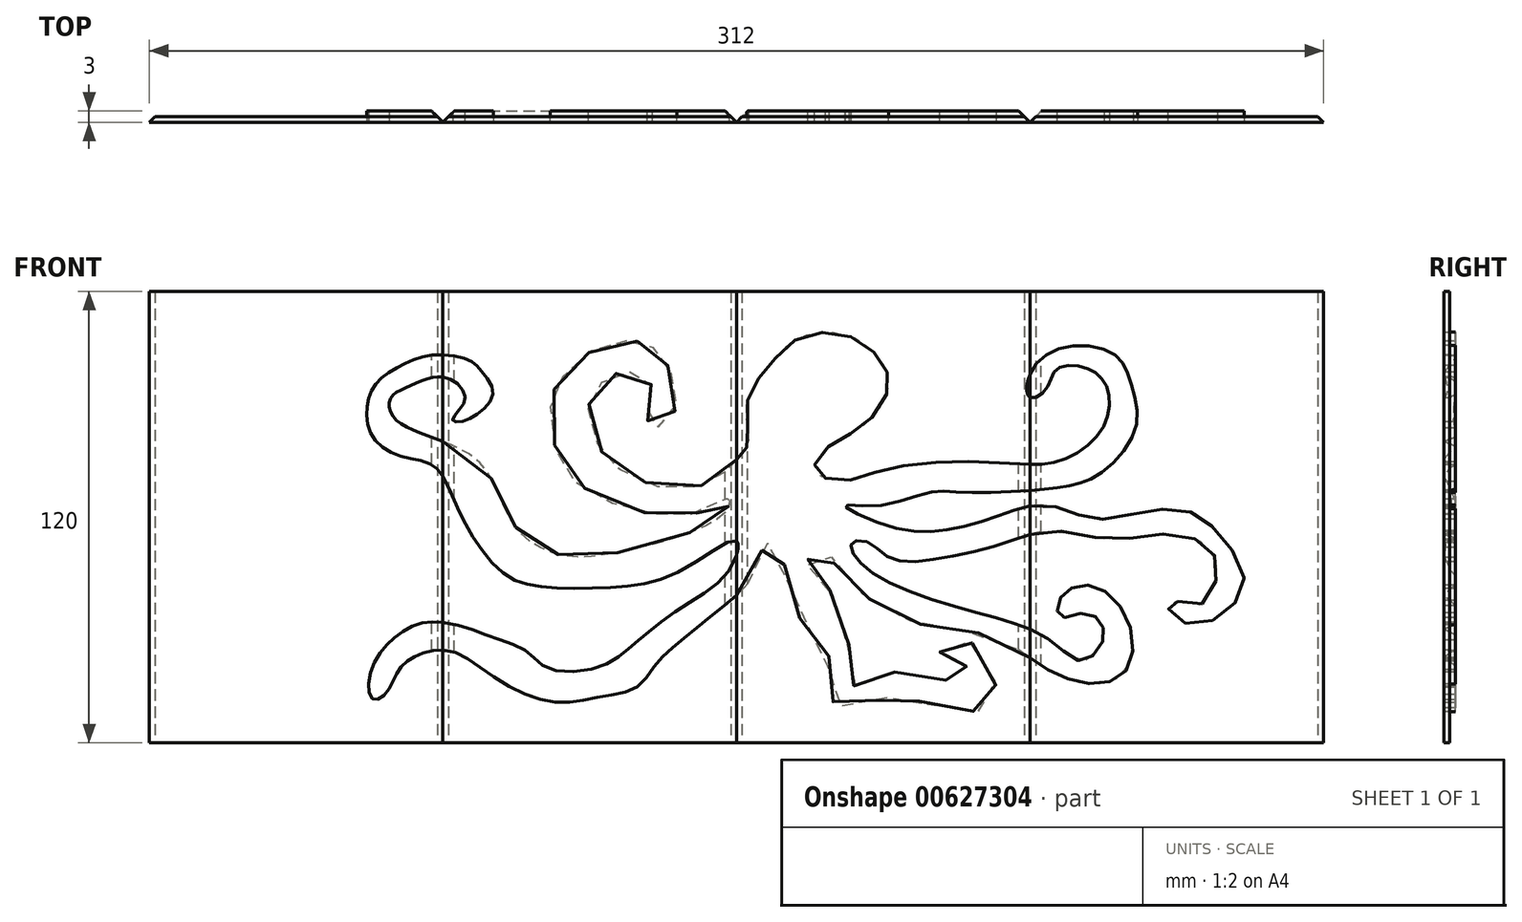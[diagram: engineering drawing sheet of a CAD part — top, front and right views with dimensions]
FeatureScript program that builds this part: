
annotation { "Feature Type Name" : "Feature", "Feature Type Description" : "" }
export const myFeature = defineFeature(function(context is Context, id is Id, definition is map)
    precondition{}
    {
        {
            var Q0;
            Q0=qCreatedBy(makeId("Top.planeOp"),FACE);
            var sketch = newSketch(context, id + "F0", { "sketchPlane" : qUnion([Q0])});
            skLineSegment(sketch, "E0", {"start": v(-73.98, 9.57) * mm, "end": v(1.02, 9.57) * mm});
            skLineSegment(sketch, "E1", {"start": v(1.02, 9.57) * mm, "end": v(2.52, 8.07) * mm});
            skLineSegment(sketch, "E2", {"start": v(2.52, 8.07) * mm, "end": v(-75.48, 8.07) * mm});
            skLineSegment(sketch, "E3", {"start": v(-75.48, 8.07) * mm, "end": v(-73.98, 9.57) * mm});
            skLineSegment(sketch, "E4.1.0.0", {"start": v(4.02, 9.57) * mm, "end": v(79.02, 9.57) * mm});
            skLineSegment(sketch, "E4.1.0.1", {"start": v(80.52, 8.07) * mm, "end": v(2.52, 8.07) * mm});
            skLineSegment(sketch, "E4.1.0.2", {"start": v(79.02, 9.57) * mm, "end": v(80.52, 8.07) * mm});
            skLineSegment(sketch, "E4.1.0.3", {"start": v(2.52, 8.07) * mm, "end": v(4.02, 9.57) * mm});
            skLineSegment(sketch, "E4.2.0.0", {"start": v(82.02, 9.57) * mm, "end": v(157.02, 9.57) * mm});
            skLineSegment(sketch, "E4.2.0.1", {"start": v(158.52, 8.07) * mm, "end": v(80.52, 8.07) * mm});
            skLineSegment(sketch, "E4.2.0.2", {"start": v(157.02, 9.57) * mm, "end": v(158.52, 8.07) * mm});
            skLineSegment(sketch, "E4.2.0.3", {"start": v(80.52, 8.07) * mm, "end": v(82.02, 9.57) * mm});
            skLineSegment(sketch, "E4.3.0.0", {"start": v(160.02, 9.57) * mm, "end": v(235.02, 9.57) * mm});
            skLineSegment(sketch, "E4.3.0.1", {"start": v(236.52, 8.07) * mm, "end": v(158.52, 8.07) * mm});
            skLineSegment(sketch, "E4.3.0.2", {"start": v(235.02, 9.57) * mm, "end": v(236.52, 8.07) * mm});
            skLineSegment(sketch, "E4.3.0.3", {"start": v(158.52, 8.07) * mm, "end": v(160.02, 9.57) * mm});
            skLineSegment(sketch, "E4.direction1", {"start": v(-75.48, 8.07) * mm, "end": v(2.52, 8.07) * mm, "construction": true});
            skSolve(sketch);
        }
        {
            var Q0;
            Q0=makeQuery(id+"F0.imprint","IMPRINT",FACE,{"disambiguationData":[TD([[makeQuery(id+"F0.imprint","IMPRINT",EDGE,{"derivedFrom":sQuery(id+"F0.wireOp",EDGE,"E0")}),-1.0]])]});
            extrude(context, id + "F1", {"entities" : qUnion([Q0]), "depth" : 120 * mm, "offsetDistance" : 25 * mm});
        }
        {
            var Q0;
            Q0=makeQuery(id+"F0.imprint","IMPRINT",FACE,{"disambiguationData":[TD([[makeQuery(id+"F0.imprint","IMPRINT",EDGE,{"derivedFrom":sQuery(id+"F0.wireOp",EDGE,"E4.1.0.0")}),-1.0]])]});
            extrude(context, id + "F2", {"entities" : qUnion([Q0]), "depth" : 120 * mm, "offsetDistance" : 25 * mm});
        }
        {
            var Q0;
            Q0=makeQuery(id+"F0.imprint","IMPRINT",FACE,{"disambiguationData":[TD([[makeQuery(id+"F0.imprint","IMPRINT",EDGE,{"derivedFrom":sQuery(id+"F0.wireOp",EDGE,"E4.2.0.0")}),-1.0]])]});
            extrude(context, id + "F3", {"entities" : qUnion([Q0]), "depth" : 120 * mm, "offsetDistance" : 25 * mm});
        }
        {
            var Q0;
            Q0=makeQuery(id+"F0.imprint","IMPRINT",FACE,{"disambiguationData":[TD([[makeQuery(id+"F0.imprint","IMPRINT",EDGE,{"derivedFrom":sQuery(id+"F0.wireOp",EDGE,"E4.3.0.0")}),-1.0]])]});
            extrude(context, id + "F4", {"entities" : qUnion([Q0]), "depth" : 120 * mm, "offsetDistance" : 25 * mm});
        }
        {
            var Q0;
            Q0=makeQuery(id+"F3.opExtrude","SWEPT_FACE",FACE,{"disambiguationData":[OSD([sQuery(id+"F0.wireOp",EDGE,"E4.2.0.1")])]});
            var sketch = newSketch(context, id + "F5", { "sketchPlane" : qUnion([Q0])});
            skPoint(sketch, "E5.174.internal.snap0", {"position": v(158.52, 60) * mm});
            skFitSpline(sketch, "E5", {"points": [v(83.62, 79.52) * mm, v(82.23, 77.34) * mm, v(78.27, 72.79) * mm, v(73.72, 69.42) * mm, v(65.4, 67.24) * mm, v(54.5, 70.02) * mm, v(46.38, 75.17) * mm, v(42.82, 81.7) * mm, v(41.23, 89.63) * mm, v(43.8, 94.78) * mm, v(48.36, 98.14) * mm, v(54.3, 98.34) * mm, v(57.67, 95.77) * mm, v(58.07, 91.21) * mm, v(56.88, 87.05) * mm, v(57.67, 84.28) * mm, v(61.83, 84.67) * mm, v(64.6, 90.22) * mm, v(63.61, 97.35) * mm, v(60.64, 102.9) * mm, v(56.68, 106.07) * mm, v(51.14, 106.86) * mm, v(42.82, 104.68) * mm, v(35.49, 98.54) * mm, v(31.72, 93) * mm, v(31.33, 83.29) * mm, v(34.9, 72.4) * mm, v(41.23, 67.04) * mm, v(54.1, 61.5) * mm, v(63.81, 60.9) * mm, v(71.93, 61.7) * mm, v(78.27, 64.87) * mm, v(78.07, 62.1) * mm, v(73.12, 58.13) * mm, v(63.22, 54.17) * mm, v(44.4, 49.81) * mm, v(34.3, 49.81) * mm, v(26.18, 53.18) * mm, v(20.83, 58.92) * mm, v(16.47, 67.84) * mm, v(10.73, 75.96) * mm, v(-2.74, 82.1) * mm, v(-10.87, 86.96) * mm, v(-11.39, 91.6) * mm, v(-7.34, 94.43) * mm, v(0, 97.18) * mm, v(5.4, 96.18) * mm, v(8.39, 91.93) * mm, v(6.64, 88.19) * mm, v(5.14, 85.7) * mm, v(7.64, 85.44) * mm, v(12.63, 88.19) * mm, v(15.88, 93.18) * mm, v(12.63, 98.93) * mm, v(9.59, 101.74) * mm, v(0, 103.13) * mm, v(-8.62, 100.35) * mm, v(-15.15, 95.6) * mm, v(-17.53, 89.67) * mm, v(-16.54, 82.15) * mm, v(-9.41, 76.4) * mm, v(0, 73.64) * mm, v(5.03, 65.52) * mm, v(9.98, 55.63) * mm, v(19.28, 44.54) * mm, v(30.17, 41.38) * mm, v(48.58, 41.38) * mm, v(66.39, 46.13) * mm, v(80.52, 53.65) * mm, v(78.4, 45.58) * mm, v(68.32, 37.53) * mm, v(57.42, 29.71) * mm, v(51.37, 24.58) * mm, v(43.73, 20.04) * mm, v(30.36, 19.8) * mm, v(25.1, 24.1) * mm, v(17.46, 27.45) * mm, v(8.15, 30.79) * mm, v(-2.12, 31.98) * mm, v(-10.95, 27.45) * mm, v(-16.68, 18.61) * mm, v(-16.2, 11.69) * mm, v(-12.86, 12.88) * mm, v(-9.52, 18.85) * mm, v(-4.98, 22.9) * mm, v(3.61, 24.58) * mm, v(11.73, 20.52) * mm, v(24.39, 12.88) * mm, v(35.61, 10.73) * mm, v(45.16, 12.4) * mm, v(54, 14.8) * mm, v(59.49, 21.24) * mm, v(66.41, 27.69) * mm, v(77.64, 36.76) * mm, v(85.04, 44.64) * mm, v(87.67, 51.8) * mm, v(89.82, 53.24) * mm, v(92.92, 48.7) * mm, v(95.07, 37) * mm, v(99.6, 31.03) * mm, v(104.86, 25.06) * mm, v(104.14, 16.7) * mm, v(106.05, 10.97) * mm, v(114.65, 9.54) * mm, v(120.86, 12.16) * mm, v(125.63, 12.64) * mm, v(130.89, 10.25) * mm, v(141.15, 8.58) * mm, v(148.08, 9.06) * mm, v(149.51, 14.07) * mm, v(147.84, 20.76) * mm, v(142.35, 26.97) * mm, v(137.1, 26.5) * mm, v(134.7, 24.58) * mm, v(134.95, 22.43) * mm, v(139.48, 22.43) * mm, v(142.11, 18.13) * mm, v(140.44, 15.03) * mm, v(134.23, 17.66) * mm, v(125.16, 19.33) * mm, v(118.23, 16.7) * mm, v(112.74, 14.8) * mm, v(109.4, 18.37) * mm, v(110.35, 25.06) * mm, v(108.2, 35.09) * mm, v(102.95, 43.2) * mm, v(99.84, 45.12) * mm, v(100.56, 51.09) * mm, v(104.14, 51.33) * mm, v(107.25, 46.31) * mm, v(112.98, 40.34) * mm, v(120.86, 35.09) * mm, v(131.36, 31.03) * mm, v(142.35, 29.6) * mm, v(152.38, 26.73) * mm, v(161.93, 20.28) * mm, v(173.87, 15.75) * mm, v(183.9, 18.97) * mm, v(185.01, 31.44) * mm, v(176.98, 41.13) * mm, v(169.5, 41.13) * mm, v(165.9, 36.98) * mm, v(166.73, 33.37) * mm, v(173.1, 34.48) * mm, v(177.53, 31.71) * mm, v(177.81, 26.73) * mm, v(172.55, 21.74) * mm, v(165.35, 26.17) * mm, v(155.38, 31.44) * mm, v(136.82, 36.7) * mm, v(116.88, 45) * mm, v(111.34, 50.82) * mm, v(111.34, 53.32) * mm, v(115.5, 53.32) * mm, v(121.31, 49.16) * mm, v(132.11, 48.6) * mm, v(150.67, 52.76) * mm, v(164.8, 56.36) * mm, v(180.3, 54.15) * mm, v(195.81, 55.53) * mm, v(206.61, 51.38) * mm, v(208, 43.34) * mm, v(202.74, 36.42) * mm, v(195.81, 37.8) * mm, v(195.81, 34.48) * mm, v(203.01, 31.44) * mm, v(212.43, 36.42) * mm, v(215.2, 45.28) * mm, v(207.72, 56.64) * mm, v(200.52, 61.62) * mm, v(188.06, 61.35) * mm, v(176.98, 59.4) * mm, v(169.23, 61.35) * mm, v(161.2, 63.29) * mm, v(149, 60) * mm, v(134.88, 56.36) * mm, v(120.48, 57.75) * mm, v(109.4, 63) * mm, v(117.71, 63) * mm, v(132.11, 66.6) * mm, v(139.31, 66.6) * mm, v(155.93, 66.89) * mm, v(168.67, 68.27) * mm, v(177.26, 71.6) * mm, v(186.67, 83.78) * mm, v(185.29, 95.69) * mm, v(181.13, 103.17) * mm, v(167.29, 105.1) * mm, v(158.52, 97.9) * mm, v(158.52, 91.81) * mm, v(162.86, 94.03) * mm, v(165.62, 99.29) * mm, v(173.66, 99.57) * mm, v(178.92, 94.58) * mm, v(178.09, 84.06) * mm, v(166.18, 74.92) * mm, v(151.5, 74.36) * mm, v(135.16, 74.64) * mm, v(118.82, 72.42) * mm, v(108.57, 69.66) * mm, v(101.37, 72.42) * mm, v(104.7, 78.52) * mm, v(113.84, 84.06) * mm, v(120.76, 93.75) * mm, v(119.1, 101.5) * mm, v(109.68, 108.43) * mm, v(96.66, 107.32) * mm, v(88.36, 99.29) * mm, v(83.37, 90.43) * mm, v(83.62, 79.52) * mm]});
            skSolve(sketch);
        }
        {
            var Q0;
            Q0=qSketchRegion(id+"F5",true);
            extrude(context, id + "F6", {"entities" : qUnion([Q0]), "oppositeDirection" : true, "depth" : 3 * mm, "offsetDistance" : 25 * mm});
        }
        {
            var Q0;
            Q0=makeQuery(id+"F2.opExtrude","CAP_FACE",FACE,{"disambiguationData":[OSD([sQuery(id+"F0.wireOp",EDGE,"E4.1.0.0"),sQuery(id+"F0.wireOp",EDGE,"E4.1.0.1"),sQuery(id+"F0.wireOp",EDGE,"E4.1.0.2"),sQuery(id+"F0.wireOp",EDGE,"E4.1.0.3")])],"isStart":false});
            var sketch = newSketch(context, id + "F7", { "sketchPlane" : qUnion([Q0])});
            skLineSegment(sketch, "E6", {"start": v(2.52, 8.07) * mm, "end": v(7.01, 12.56) * mm});
            skLineSegment(sketch, "E7", {"start": v(2.52, 8.07) * mm, "end": v(-1.98, 12.56) * mm});
            skLineSegment(sketch, "E8", {"start": v(-1.98, 12.56) * mm, "end": v(7.01, 12.56) * mm});
            skLineSegment(sketch, "E9.1.0.0", {"start": v(76.02, 12.56) * mm, "end": v(85.01, 12.56) * mm});
            skLineSegment(sketch, "E9.1.0.1", {"start": v(80.52, 8.07) * mm, "end": v(76.02, 12.56) * mm});
            skLineSegment(sketch, "E9.1.0.2", {"start": v(80.52, 8.07) * mm, "end": v(85.01, 12.56) * mm});
            skLineSegment(sketch, "E9.2.0.0", {"start": v(154.02, 12.56) * mm, "end": v(163.01, 12.56) * mm});
            skLineSegment(sketch, "E9.2.0.1", {"start": v(158.52, 8.07) * mm, "end": v(154.02, 12.56) * mm});
            skLineSegment(sketch, "E9.2.0.2", {"start": v(158.52, 8.07) * mm, "end": v(163.01, 12.56) * mm});
            skLineSegment(sketch, "E9.direction1", {"start": v(2.52, 8.07) * mm, "end": v(80.52, 8.07) * mm, "construction": true});
            skSolve(sketch);
        }
        {
            var Q0;
            {var subQ0=sQuery(id+"F7.wireOp",EDGE,"E7");Q0=makeQuery(id+"F7.imprint","IMPRINT",FACE,{"disambiguationData":[TD([[makeQuery(id+"F7.imprint","IMPRINT",EDGE,{"derivedFrom":subQ0}),-1.0]])]});}
            var Q1;
            {var subQ0=sQuery(id+"F7.wireOp",EDGE,"E9.1.0.0");Q1=makeQuery(id+"F7.imprint","IMPRINT",FACE,{"disambiguationData":[TD([[makeQuery(id+"F7.imprint","IMPRINT",EDGE,{"derivedFrom":subQ0}),-1.0]])]});}
            var Q2;
            Q2=makeQuery(id+"F7.imprint","IMPRINT",FACE,{"disambiguationData":[TD([[makeQuery(id+"F7.imprint","IMPRINT",EDGE,{"derivedFrom":sQuery(id+"F7.wireOp",EDGE,"E9.2.0.0")}),-1.0]])]});
            extrude(context, id + "F8", {"entities" : qUnion([Q0, Q1, Q2]), "operationType" : NewBodyOperationType.REMOVE, "endBound" : BoundingType.THROUGH_ALL, "oppositeDirection" : true, "depth" : 25 * mm, "offsetDistance" : 25 * mm});
        }
    });
